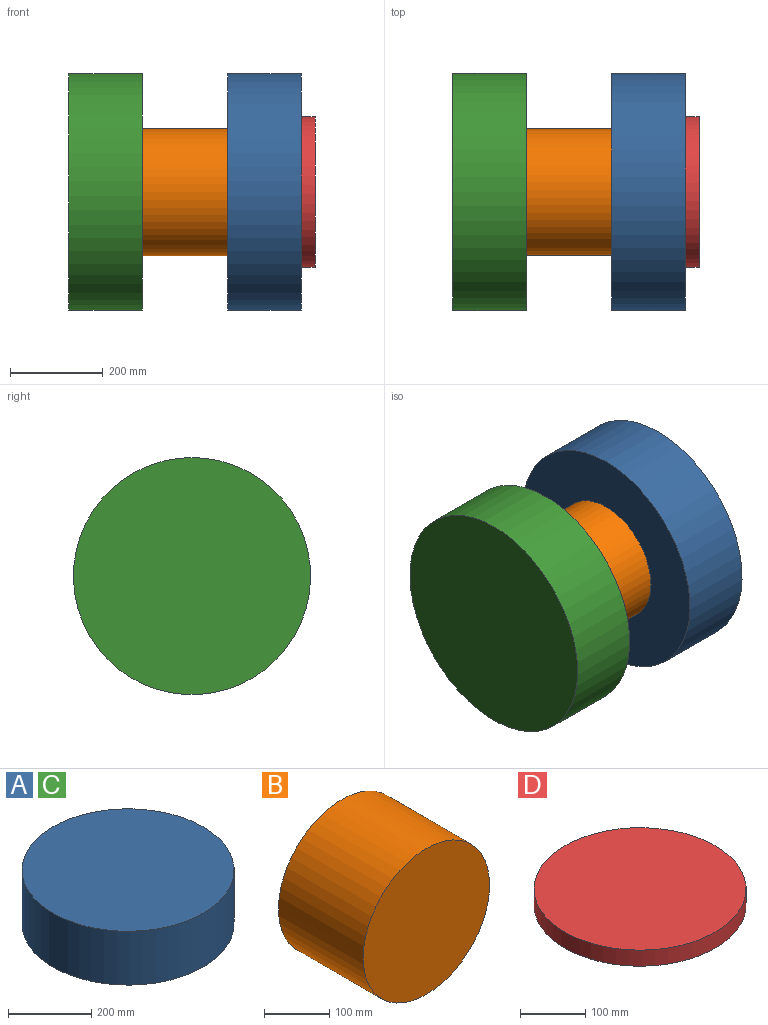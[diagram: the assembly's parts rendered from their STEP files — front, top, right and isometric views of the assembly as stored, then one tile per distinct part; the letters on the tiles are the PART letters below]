
ASSEMBLY  parts=4 mates=3
PART A: 3 faces, bbox 510x510x158.4 mm
  f0: cylinder r=255mm len=510mm, axis (0,0,-1), area 253790.4mm2, adj f1,f2
  f1: plane 510x510mm, normal (0,0,1), area 204282.1mm2, adj f0
  f2: plane 510x510mm, normal (0,0,-1), area 204282.1mm2, adj f0
PART B: 3 faces, bbox 273.1x183.2x273.1 mm
  f0: cylinder r=136.55mm len=273.1mm, axis (0,1,0), area 157179.9mm2, adj f1,f2
  f1: plane 273.1x273.1mm, normal (0,-1,0), area 58577.8mm2, adj f0
  f2: plane 273.1x273.1mm, normal (0,1,0), area 58577.8mm2, adj f0
PART C: same geometry as A
PART D: 3 faces, bbox 323.9x323.9x30 mm
  f0: cylinder r=161.95mm len=323.9mm, axis (0,0,-1), area 30526.9mm2, adj f1,f2
  f1: plane 323.9x323.9mm, normal (0,0,1), area 82397.1mm2, adj f0
  f2: plane 323.9x323.9mm, normal (0,0,-1), area 82397.1mm2, adj f0
PLACE A rot(axis=(0,-1,0),90deg) t=(-15,0,0)mm
PLACE B rot(axis=(-0.58,0.58,0.58),120deg) t=(-356.6,0,0)mm
PLACE C rot(axis=(0,-1,0),90deg) t=(-356.6,0,0)mm
PLACE D rot(axis=(0,-1,0),90deg) t=(15,0,0)mm
MATE fastened A.f0 <-> D.f0  axis (1,0,0) through (-15,0,0)mm
MATE fastened B.f0 <-> A.f0  axis (1,0,0) through (-173.4,0,0)mm
MATE fastened C.f0 <-> B.f0  axis (1,0,0) through (-356.6,0,0)mm
